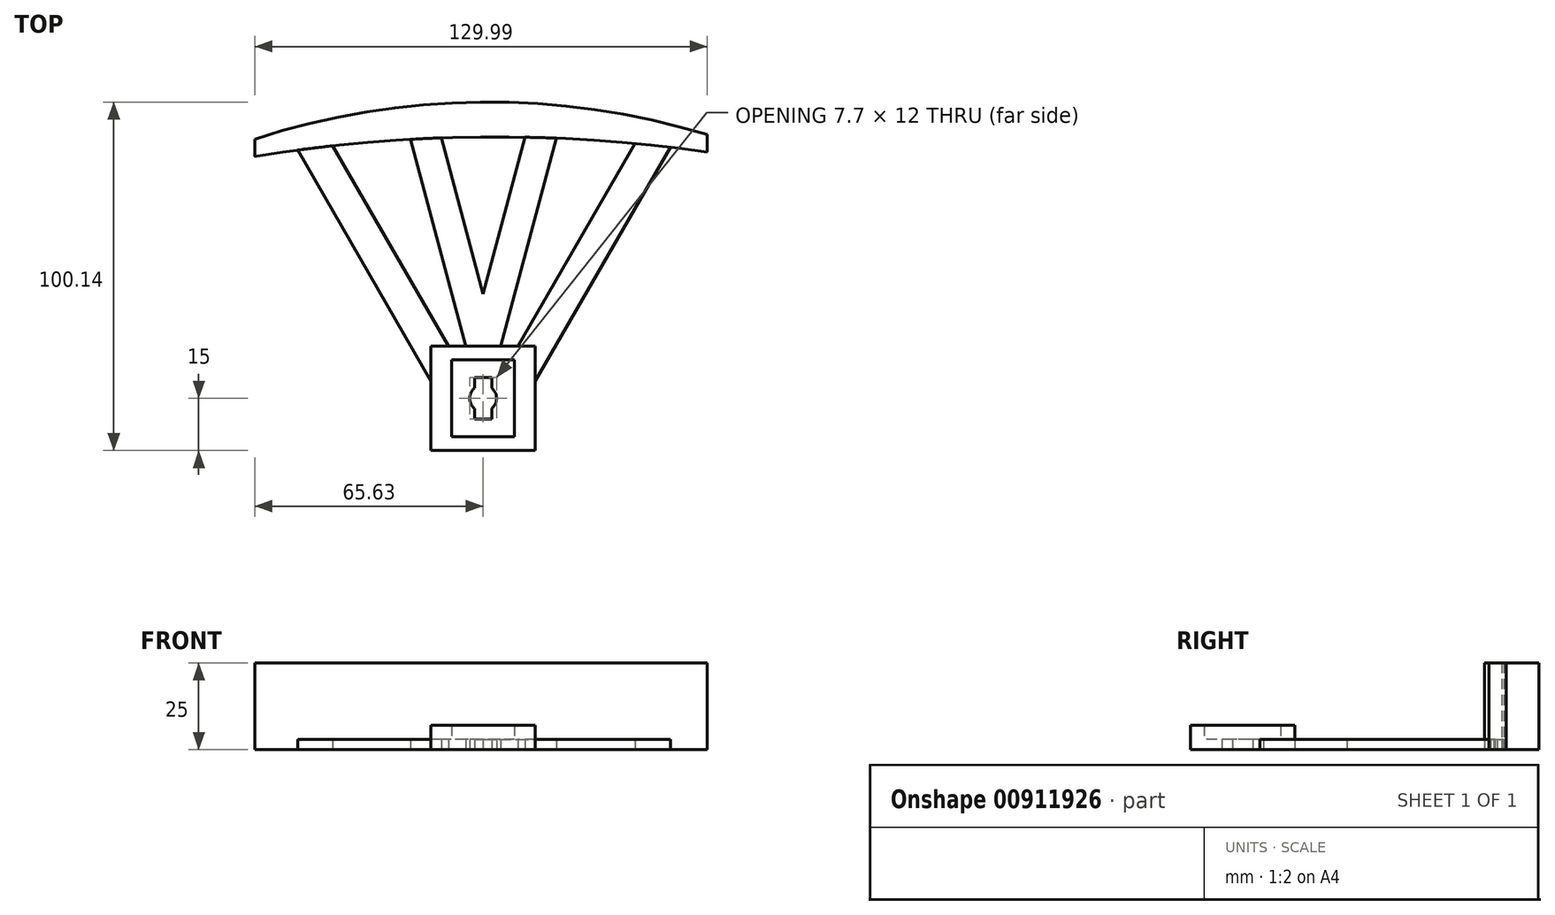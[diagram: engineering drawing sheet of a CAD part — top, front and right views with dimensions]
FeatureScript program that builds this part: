
annotation { "Feature Type Name" : "Feature", "Feature Type Description" : "" }
export const myFeature = defineFeature(function(context is Context, id is Id, definition is map)
    precondition{}
    {
        {
            var Q0;
            Q0=qCreatedBy(makeId("Top.planeOp"),FACE);
            var sketch = newSketch(context, id + "F0", { "sketchPlane" : qUnion([Q0])});
            skLineSegment(sketch, "E0.bottom", {"start": v(15, 15) * mm, "end": v(-15, 15) * mm});
            skLineSegment(sketch, "E0.top", {"start": v(15, -15) * mm, "end": v(-15, -15) * mm});
            skLineSegment(sketch, "E0.left", {"start": v(15, 15) * mm, "end": v(15, -15) * mm});
            skLineSegment(sketch, "E0.right", {"start": v(-15, 15) * mm, "end": v(-15, -15) * mm});
            skPoint(sketch, "E0.middle", {"position": v(0, 0) * mm});
            skPoint(sketch, "E1", {"position": v(-65.63, 74.5) * mm});
            skPoint(sketch, "E2", {"position": v(64.36, 75.77) * mm});
            skArc(sketch, "E3", {"start": v(64.36, 75.77) * mm, "mid": v(-0.73, 85.13) * mm, "end": v(-65.63, 74.5) * mm});
            skPoint(sketch, "E4", {"position": v(-15, 5) * mm});
            skPoint(sketch, "E5", {"position": v(-10, 15) * mm});
            skPoint(sketch, "E6", {"position": v(15, 5) * mm});
            skPoint(sketch, "E7", {"position": v(10, 15) * mm});
            skPoint(sketch, "E8", {"position": v(-5, 15) * mm});
            skPoint(sketch, "E9", {"position": v(5, 15) * mm});
            skLineSegment(sketch, "E10", {"start": v(-5, 15) * mm, "end": v(-20.92, 74.42) * mm});
            skLineSegment(sketch, "E11", {"start": v(5, 15) * mm, "end": v(21.01, 74.76) * mm});
            skPoint(sketch, "E12", {"position": v(0, 30) * mm});
            skLineSegment(sketch, "E13", {"start": v(0, 30) * mm, "end": v(-12.01, 74.84) * mm});
            skLineSegment(sketch, "E14", {"start": v(0, 30) * mm, "end": v(12.07, 75.03) * mm});
            skLineSegment(sketch, "E15.bottom", {"start": v(9, 11) * mm, "end": v(-9, 11) * mm});
            skLineSegment(sketch, "E15.top", {"start": v(9, -11) * mm, "end": v(-9, -11) * mm});
            skLineSegment(sketch, "E15.left", {"start": v(9, 11) * mm, "end": v(9, -11) * mm});
            skLineSegment(sketch, "E15.right", {"start": v(-9, 11) * mm, "end": v(-9, -11) * mm});
            skCircle(sketch, "E16", {"center": v(0, 0) * mm, "radius": 3.85 * mm});
            skPoint(sketch, "E17", {"position": v(-65.63, 69.5) * mm});
            skPoint(sketch, "E18", {"position": v(64.36, 70.77) * mm});
            skArc(sketch, "E19", {"start": v(64.36, 70.77) * mm, "mid": v(-0.69, 75.1) * mm, "end": v(-65.63, 69.5) * mm});
            skLineSegment(sketch, "E20", {"start": v(64.36, 75.77) * mm, "end": v(64.36, 70.77) * mm});
            skLineSegment(sketch, "E21", {"start": v(-65.63, 74.5) * mm, "end": v(-65.63, 69.5) * mm});
            skLineSegment(sketch, "E22", {"start": v(-15, 5) * mm, "end": v(-53.3, 71.33) * mm});
            skLineSegment(sketch, "E23", {"start": v(-10, 15) * mm, "end": v(-43.23, 72.56) * mm});
            skLineSegment(sketch, "E24", {"start": v(15, 5) * mm, "end": v(53.77, 72.16) * mm});
            skLineSegment(sketch, "E25", {"start": v(10, 15) * mm, "end": v(43.62, 73.23) * mm});
            skLineSegment(sketch, "E26.bottom", {"start": v(-2.5, 6) * mm, "end": v(2.5, 6) * mm});
            skLineSegment(sketch, "E26.top", {"start": v(-2.5, -6) * mm, "end": v(2.5, -6) * mm});
            skLineSegment(sketch, "E26.left", {"start": v(-2.5, 6) * mm, "end": v(-2.5, -6) * mm});
            skLineSegment(sketch, "E26.right", {"start": v(2.5, 6) * mm, "end": v(2.5, -6) * mm});
            skSolve(sketch);
        }
        {
            var Q0;
            {var subQ1=sQuery(id+"F0.wireOp",EDGE,"E0.top");Q0=makeQuery(id+"F0.imprint","IMPRINT",FACE,{"disambiguationData":[TD([[makeQuery(id+"F0.imprint","IMPRINT",EDGE,{"derivedFrom":subQ1}),-1.0]])]});}
            extrude(context, id + "F1", {"entities" : qUnion([Q0]), "depth" : 7 * mm, "offsetDistance" : 25 * mm});
        }
        {
            var Q0;
            Q0=makeQuery(id+"F0.imprint","IMPRINT",FACE,{"disambiguationData":[TD([[makeQuery(id+"F0.imprint","IMPRINT",EDGE,{"derivedFrom":sQuery(id+"F0.wireOp",EDGE,"E15.bottom")}),1.0]])]});
            extrude(context, id + "F2", {"entities" : qUnion([Q0]), "operationType" : NewBodyOperationType.ADD, "depth" : 3 * mm, "offsetDistance" : 25 * mm});
        }
        {
            var Q0;
            {var subQ0=sQuery(id+"F0.wireOp",EDGE,"E22");Q0=makeQuery(id+"F0.imprint","IMPRINT",FACE,{"disambiguationData":[TD([[makeQuery(id+"F0.imprint","IMPRINT",EDGE,{"derivedFrom":subQ0}),-1.0]])]});}
            var Q1;
            {var subQ1=sQuery(id+"F0.wireOp",EDGE,"E10");Q1=makeQuery(id+"F0.imprint","IMPRINT",FACE,{"disambiguationData":[TD([[makeQuery(id+"F0.imprint","IMPRINT",EDGE,{"derivedFrom":subQ1}),-1.0]])]});}
            var Q2;
            {var subQ0=sQuery(id+"F0.wireOp",EDGE,"E24");Q2=makeQuery(id+"F0.imprint","IMPRINT",FACE,{"disambiguationData":[TD([[makeQuery(id+"F0.imprint","IMPRINT",EDGE,{"derivedFrom":subQ0}),1.0]])]});}
            extrude(context, id + "F3", {"entities" : qUnion([Q0, Q1, Q2]), "operationType" : NewBodyOperationType.ADD, "depth" : 3 * mm, "offsetDistance" : 25 * mm});
        }
        {
            var Q0;
            Q0=makeQuery(id+"F0.imprint","IMPRINT",FACE,{"disambiguationData":[TD([[makeQuery(id+"F0.imprint","IMPRINT",EDGE,{"derivedFrom":sQuery(id+"F0.wireOp",EDGE,"E3")}),1.0]])]});
            extrude(context, id + "F4", {"entities" : qUnion([Q0]), "operationType" : NewBodyOperationType.ADD, "depth" : 25 * mm, "offsetDistance" : 25 * mm});
        }
    });
